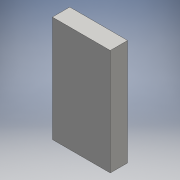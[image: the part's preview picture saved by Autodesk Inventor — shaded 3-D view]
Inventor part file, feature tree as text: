
AUTODESK INVENTOR PART (.ipt)
format: ipt  version: 2016 (Build 200138000, 138)  size: 85,504 bytes
history: native  units: mm
features: other x1, extrude x1, sketch x1
ambient origin geometry x8: Origin, YZ Plane, XZ Plane, XY Plane, X Axis, Y Axis, Z Axis, Center Point
bodies: Body1 (feature_tree)
feature tree (3):
  other  "Bryła1"
  extrude  "Wyciągnięcie proste1"  Depth=55.0mm
  sketch  "Szkic1"
